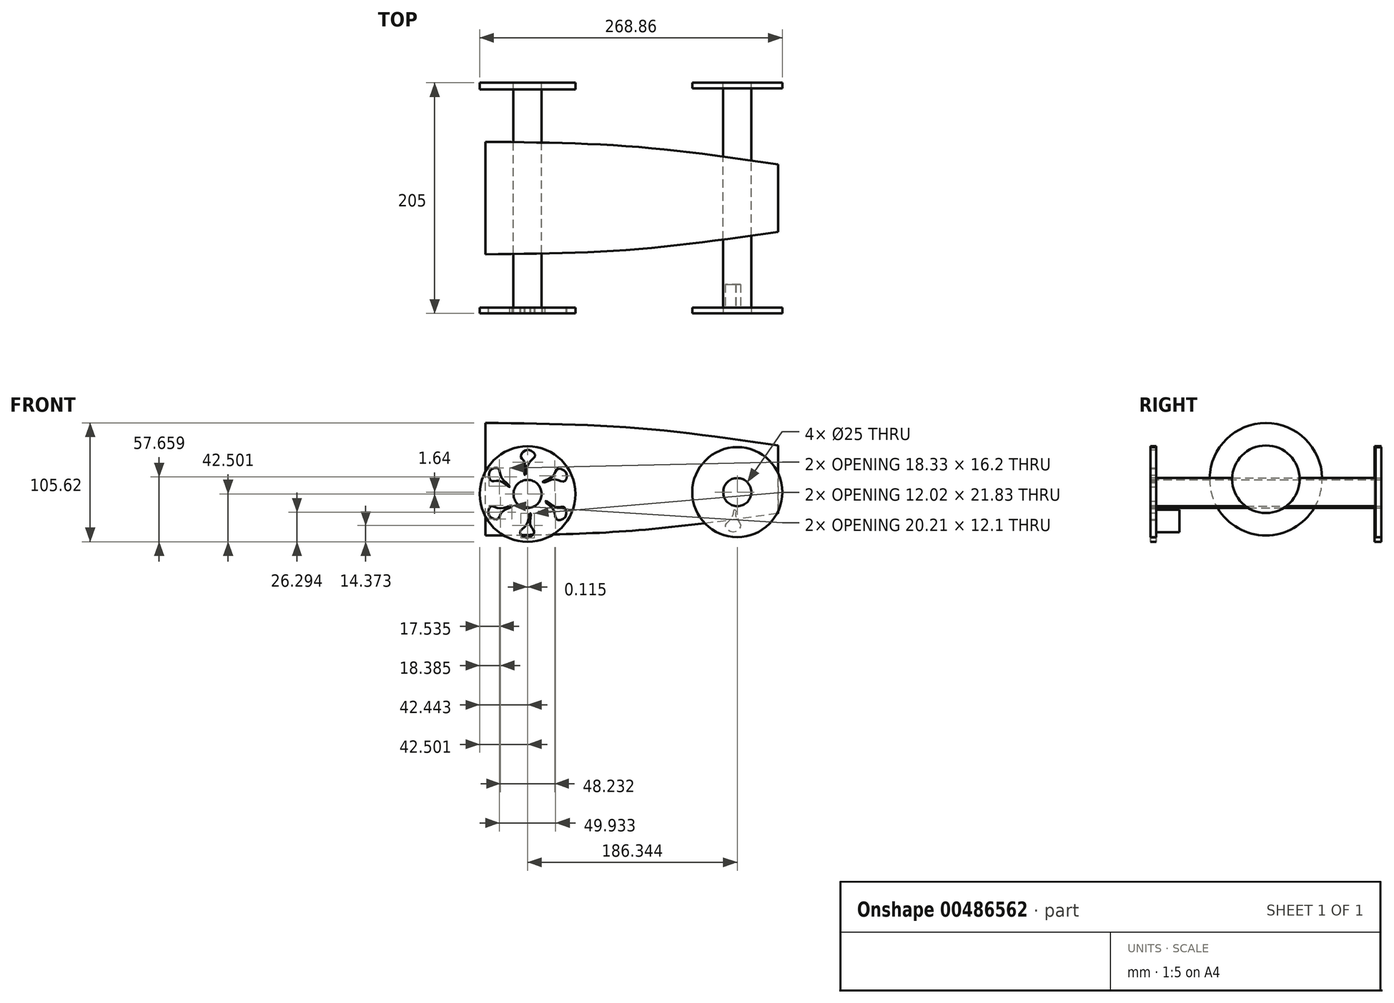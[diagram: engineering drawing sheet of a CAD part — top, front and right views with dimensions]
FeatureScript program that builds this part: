
annotation { "Feature Type Name" : "Feature", "Feature Type Description" : "" }
export const myFeature = defineFeature(function(context is Context, id is Id, definition is map)
    precondition{}
    {
        {
            var Q0;
            Q0=qCreatedBy(makeId("Right.planeOp"),FACE);
            cPlane(context, id + "F0", {"entities" : qUnion([Q0]), "cplaneType" : CPlaneType.OFFSET, "offset" : 130 * mm, "width" : 150 * mm, "height" : 150 * mm});
        }
        {
            var Q0;
            Q0=qCreatedBy(id+"F0.planeOp",FACE);
            cPlane(context, id + "F1", {"entities" : qUnion([Q0]), "cplaneType" : CPlaneType.OFFSET, "offset" : 130 * mm, "width" : 150 * mm, "height" : 150 * mm});
        }
        {
            var Q0;
            Q0=qCreatedBy(makeId("Right.planeOp"),FACE);
            var sketch = newSketch(context, id + "F2", { "sketchPlane" : qUnion([Q0])});
            skCircle(sketch, "E0", {"center": v(0, 0) * mm, "radius": 50 * mm});
            skSolve(sketch);
        }
        {
            var Q0;
            Q0=qCreatedBy(id+"F0.planeOp",FACE);
            var sketch = newSketch(context, id + "F3", { "sketchPlane" : qUnion([Q0])});
            skCircle(sketch, "E1", {"center": v(0, 0) * mm, "radius": 45.8 * mm});
            skSolve(sketch);
        }
        {
            var Q0;
            Q0=qCreatedBy(id+"F1.planeOp",FACE);
            var sketch = newSketch(context, id + "F4", { "sketchPlane" : qUnion([Q0])});
            skCircle(sketch, "E2", {"center": v(0, 0) * mm, "radius": 30 * mm});
            skSolve(sketch);
        }
        {
            var Q0;
            Q0=makeQuery(id+"F2.imprint","IMPRINT",FACE,{"disambiguationData":[TD([[makeQuery(id+"F2.imprint","IMPRINT",EDGE,{"derivedFrom":sQuery(id+"F2.wireOp",EDGE,"E0")}),1.0]])]});
            var Q1;
            Q1=makeQuery(id+"F3.imprint","IMPRINT",FACE,{"disambiguationData":[TD([[makeQuery(id+"F3.imprint","IMPRINT",EDGE,{"derivedFrom":sQuery(id+"F3.wireOp",EDGE,"E1")}),1.0]])]});
            var Q2;
            Q2=makeQuery(id+"F4.imprint","IMPRINT",FACE,{"disambiguationData":[TD([[makeQuery(id+"F4.imprint","IMPRINT",EDGE,{"derivedFrom":sQuery(id+"F4.wireOp",EDGE,"E2")}),1.0]])]});
            loft(context, id + "F5", {"sheetProfilesArray" : [{ "sheetProfileEntities" : qUnion([Q0]) }, { "sheetProfileEntities" : qUnion([Q1]) }, { "sheetProfileEntities" : qUnion([Q2]) }]});
        }
        {
            var Q0;
            Q0=qCreatedBy(makeId("Front.planeOp"),FACE);
            var sketch = newSketch(context, id + "F6", { "sketchPlane" : qUnion([Q0])});
            skCircle(sketch, "E3", {"center": v(37.33, -13.12) * mm, "radius": 12.5 * mm});
            skSolve(sketch);
        }
        {
            var Q0;
            Q0=makeQuery(id+"F6.imprint","IMPRINT",FACE,{"disambiguationData":[TD([[makeQuery(id+"F6.imprint","IMPRINT",EDGE,{"derivedFrom":sQuery(id+"F6.wireOp",EDGE,"E3")}),1.0]])]});
            extrude(context, id + "F7", {"entities" : qUnion([Q0]), "endBound" : BoundingType.SYMMETRIC, "depth" : 205 * mm});
        }
        {
            var Q0;
            Q0=qCreatedBy(makeId("Front.planeOp"),FACE);
            var sketch = newSketch(context, id + "F8", { "sketchPlane" : qUnion([Q0])});
            skCircle(sketch, "E4", {"center": v(223.68, -11.48) * mm, "radius": 12.5 * mm});
            skSolve(sketch);
        }
        {
            var Q0;
            Q0=makeQuery(id+"F8.imprint","IMPRINT",FACE,{"disambiguationData":[TD([[makeQuery(id+"F8.imprint","IMPRINT",EDGE,{"derivedFrom":sQuery(id+"F8.wireOp",EDGE,"E4")}),1.0]])]});
            extrude(context, id + "F9", {"entities" : qUnion([Q0]), "endBound" : BoundingType.SYMMETRIC, "depth" : 205 * mm});
        }
        {
            var Q0;
            Q0=makeQuery(id+"F7.opExtrude","CAP_FACE",FACE,{"disambiguationData":[OSD([sQuery(id+"F6.wireOp",EDGE,"E3")])],"isStart":true});
            var sketch = newSketch(context, id + "F10", { "sketchPlane" : qUnion([Q0])});
            skCircle(sketch, "E5", {"center": v(-37.33, -13.12) * mm, "radius": 42.5 * mm});
            skSolve(sketch);
        }
        {
            var Q0;
            Q0=makeQuery(id+"F10.imprint","IMPRINT",FACE,{"disambiguationData":[TD([[makeQuery(id+"F10.imprint","IMPRINT",EDGE,{"derivedFrom":sQuery(id+"F10.wireOp",EDGE,"E5")}),1.0]])]});
            extrude(context, id + "F11", {"entities" : qUnion([Q0]), "oppositeDirection" : true, "depth" : 6 * mm});
        }
        {
            var Q0;
            Q0=makeQuery(id+"F9.opExtrude","CAP_FACE",FACE,{"disambiguationData":[OSD([sQuery(id+"F8.wireOp",EDGE,"E4")])],"isStart":true});
            var sketch = newSketch(context, id + "F12", { "sketchPlane" : qUnion([Q0])});
            skCircle(sketch, "E6", {"center": v(-223.68, -11.48) * mm, "radius": 40 * mm});
            skSolve(sketch);
        }
        {
            var Q0;
            Q0=makeQuery(id+"F12.imprint","IMPRINT",FACE,{"disambiguationData":[TD([[makeQuery(id+"F12.imprint","IMPRINT",EDGE,{"derivedFrom":sQuery(id+"F12.wireOp",EDGE,"E6")}),1.0]])]});
            extrude(context, id + "F13", {"entities" : qUnion([Q0]), "oppositeDirection" : true, "depth" : 5 * mm});
        }
        {
            var Q0;
            Q0=makeQuery(id+"F7.opExtrude","CAP_FACE",FACE,{"disambiguationData":[OSD([sQuery(id+"F6.wireOp",EDGE,"E3")])],"isStart":false});
            var sketch = newSketch(context, id + "F14", { "sketchPlane" : qUnion([Q0])});
            skCircle(sketch, "E7", {"center": v(37.33, -13.12) * mm, "radius": 42.5 * mm});
            skSolve(sketch);
        }
        {
            var Q0;
            Q0=makeQuery(id+"F14.imprint","IMPRINT",FACE,{"disambiguationData":[TD([[makeQuery(id+"F14.imprint","IMPRINT",EDGE,{"derivedFrom":sQuery(id+"F14.wireOp",EDGE,"E7")}),1.0]])]});
            extrude(context, id + "F15", {"entities" : qUnion([Q0]), "oppositeDirection" : true, "depth" : 5 * mm});
        }
        {
            var Q0;
            Q0=makeQuery(id+"F9.opExtrude","CAP_FACE",FACE,{"disambiguationData":[OSD([sQuery(id+"F8.wireOp",EDGE,"E4")])],"isStart":false});
            var sketch = newSketch(context, id + "F16", { "sketchPlane" : qUnion([Q0])});
            skCircle(sketch, "E8", {"center": v(223.68, -11.48) * mm, "radius": 40.01 * mm});
            skSolve(sketch);
        }
        {
            var Q0;
            Q0=makeQuery(id+"F16.imprint","IMPRINT",FACE,{"disambiguationData":[TD([[makeQuery(id+"F16.imprint","IMPRINT",EDGE,{"derivedFrom":sQuery(id+"F16.wireOp",EDGE,"E8")}),1.0]])]});
            extrude(context, id + "F17", {"entities" : qUnion([Q0]), "oppositeDirection" : true, "depth" : 5 * mm});
        }
        {
            var Q0;
            Q0=makeQuery(id+"F15.opExtrude","CAP_FACE",FACE,{"disambiguationData":[OSD([sQuery(id+"F6.wireOp",EDGE,"E3"),sQuery(id+"F14.wireOp",EDGE,"E7")])],"isStart":true});
            var sketch = newSketch(context, id + "F18", { "sketchPlane" : qUnion([Q0])});
            skFitSpline(sketch, "E9", {"points": [v(39.12, -30.33) * mm, v(36.59, -40.21) * mm, v(30.62, -47.07) * mm, v(36.85, -52.3) * mm, v(43.34, -46.77) * mm, v(39.82, -40.8) * mm, v(40, -30.33) * mm, v(39.12, -30.33) * mm]});
            skSolve(sketch);
        }
        {
            var Q0;
            Q0=makeQuery(id+"F18.imprint","IMPRINT",FACE,{"disambiguationData":[TD([[makeQuery(id+"F18.imprint","IMPRINT",EDGE,{"derivedFrom":sQuery(id+"F18.wireOp",EDGE,"E9")}),1.0]])]});
            extrude(context, id + "F19", {"entities" : qUnion([Q0]), "oppositeDirection" : true, "depth" : 50 * mm});
        }
        {
            var Q0;
            Q0=makeQuery(id+"F19.opExtrude","SWEPT_BODY",BODY,{"disambiguationData":[OSD([sQuery(id+"F18.wireOp",EDGE,"E9")])]});
            var Q1;
            Q1=makeQuery(id+"F7.opExtrude","CAP_EDGE",EDGE,{"disambiguationData":[OSD([sQuery(id+"F6.wireOp",EDGE,"E3")])],"isStart":false});
            circularPattern(context, id + "F20", {"entities" : qUnion([Q0]), "axis" : qUnion([Q1]), "angle" : 360 * degree, "instanceCount" : 6, "equalSpace" : true});
        }
        {
            var Q0;
            Q0=makeQuery(id+"F20.opPattern","COPY",BODY,{"derivedFrom":makeQuery(id+"F19.opExtrude","SWEPT_BODY",BODY,{"disambiguationData":[OSD([sQuery(id+"F18.wireOp",EDGE,"E9")])]}),"instanceName":"5"});
            var Q1;
            Q1=makeQuery(id+"F20.opPattern","COPY",BODY,{"derivedFrom":makeQuery(id+"F19.opExtrude","SWEPT_BODY",BODY,{"disambiguationData":[OSD([sQuery(id+"F18.wireOp",EDGE,"E9")])]}),"instanceName":"4"});
            var Q2;
            Q2=makeQuery(id+"F20.opPattern","COPY",BODY,{"derivedFrom":makeQuery(id+"F19.opExtrude","SWEPT_BODY",BODY,{"disambiguationData":[OSD([sQuery(id+"F18.wireOp",EDGE,"E9")])]}),"instanceName":"3"});
            var Q3;
            Q3=makeQuery(id+"F20.opPattern","COPY",BODY,{"derivedFrom":makeQuery(id+"F19.opExtrude","SWEPT_BODY",BODY,{"disambiguationData":[OSD([sQuery(id+"F18.wireOp",EDGE,"E9")])]}),"instanceName":"2"});
            var Q4;
            Q4=makeQuery(id+"F20.opPattern","COPY",BODY,{"derivedFrom":makeQuery(id+"F19.opExtrude","SWEPT_BODY",BODY,{"disambiguationData":[OSD([sQuery(id+"F18.wireOp",EDGE,"E9")])]}),"instanceName":"1"});
            var Q5;
            Q5=makeQuery(id+"F19.opExtrude","SWEPT_BODY",BODY,{"disambiguationData":[OSD([sQuery(id+"F18.wireOp",EDGE,"E9")])]});
            var Q6;
            Q6=makeQuery(id+"F15.opExtrude","SWEPT_BODY",BODY,{"disambiguationData":[OSD([sQuery(id+"F6.wireOp",EDGE,"E3"),sQuery(id+"F14.wireOp",EDGE,"E7")])]});
            booleanBodies(context, id + "F21", {"operationType" : BooleanOperationType.SUBTRACTION, "tools" : qUnion([Q0, Q1, Q2, Q3, Q4, Q5]), "targets" : qUnion([Q6])});
        }
        {
            var Q0;
            Q0=makeQuery(id+"F17.opExtrude","CAP_FACE",FACE,{"disambiguationData":[OSD([sQuery(id+"F8.wireOp",EDGE,"E4"),sQuery(id+"F16.wireOp",EDGE,"E8")])],"isStart":true});
            var sketch = newSketch(context, id + "F22", { "sketchPlane" : qUnion([Q0])});
            skFitSpline(sketch, "E10", {"points": [v(221, -27.2) * mm, v(222.18, -27.53) * mm, v(222.26, -33.8) * mm, v(226.65, -41.14) * mm, v(220.18, -47.06) * mm, v(213.1, -41.33) * mm, v(218.98, -34.16) * mm, v(221, -27.2) * mm]});
            skSolve(sketch);
        }
        {
            var Q0;
            Q0 = qSketchRegion(id + "F22", true);
            extrude(context, id + "F23", {"entities" : qUnion([Q0]), "operationType" : NewBodyOperationType.ADD, "oppositeDirection" : true, "depth" : 25.8 * mm});
        }
    });
